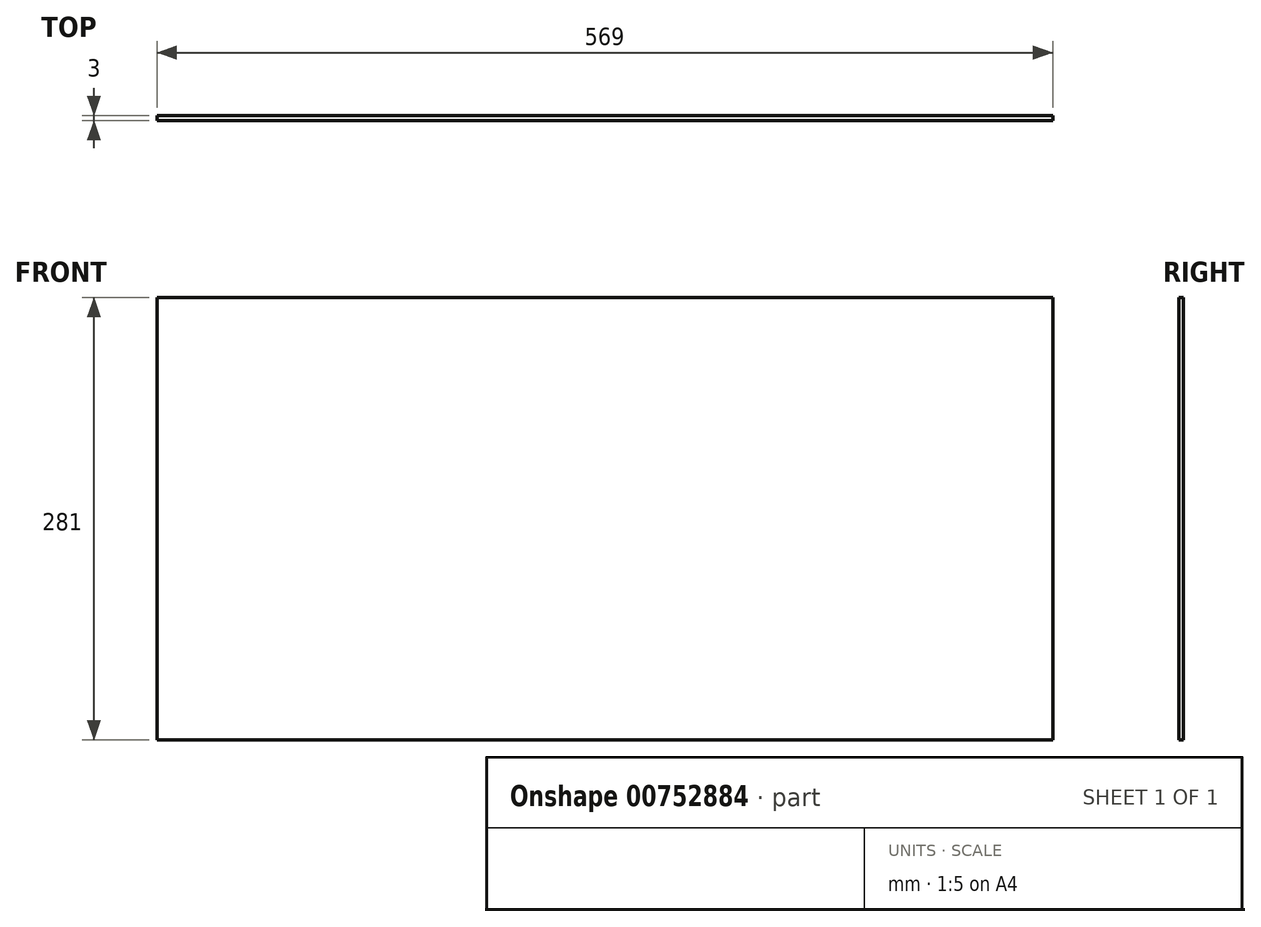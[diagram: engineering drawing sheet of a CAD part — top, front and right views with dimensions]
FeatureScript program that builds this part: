
annotation { "Feature Type Name" : "Feature", "Feature Type Description" : "" }
export const myFeature = defineFeature(function(context is Context, id is Id, definition is map)
    precondition{}
    {
        {
            var Q0;
            Q0=qCreatedBy(makeId("Front.planeOp"),FACE);
            var sketch = newSketch(context, id + "F0", { "sketchPlane" : qUnion([Q0])});
            skLineSegment(sketch, "E0.bottom", {"start": v(-284.5, 140.5) * mm, "end": v(284.5, 140.5) * mm});
            skLineSegment(sketch, "E0.top", {"start": v(-284.5, -140.5) * mm, "end": v(284.5, -140.5) * mm});
            skLineSegment(sketch, "E0.left", {"start": v(-284.5, 140.5) * mm, "end": v(-284.5, -140.5) * mm});
            skLineSegment(sketch, "E0.right", {"start": v(284.5, 140.5) * mm, "end": v(284.5, -140.5) * mm});
            skPoint(sketch, "E0.middle", {"position": v(0, 0) * mm});
            skSolve(sketch);
        }
        {
            var Q0;
            Q0=makeQuery(id+"F0.imprint","IMPRINT",FACE,{"disambiguationData":[TD([[makeQuery(id+"F0.imprint","IMPRINT",EDGE,{"derivedFrom":sQuery(id+"F0.wireOp",EDGE,"E0.bottom")}),-1.0]])]});
            extrude(context, id + "F1", {"entities" : qUnion([Q0]), "depth" : 3 * mm, "offsetDistance" : 25 * mm});
        }
    });
